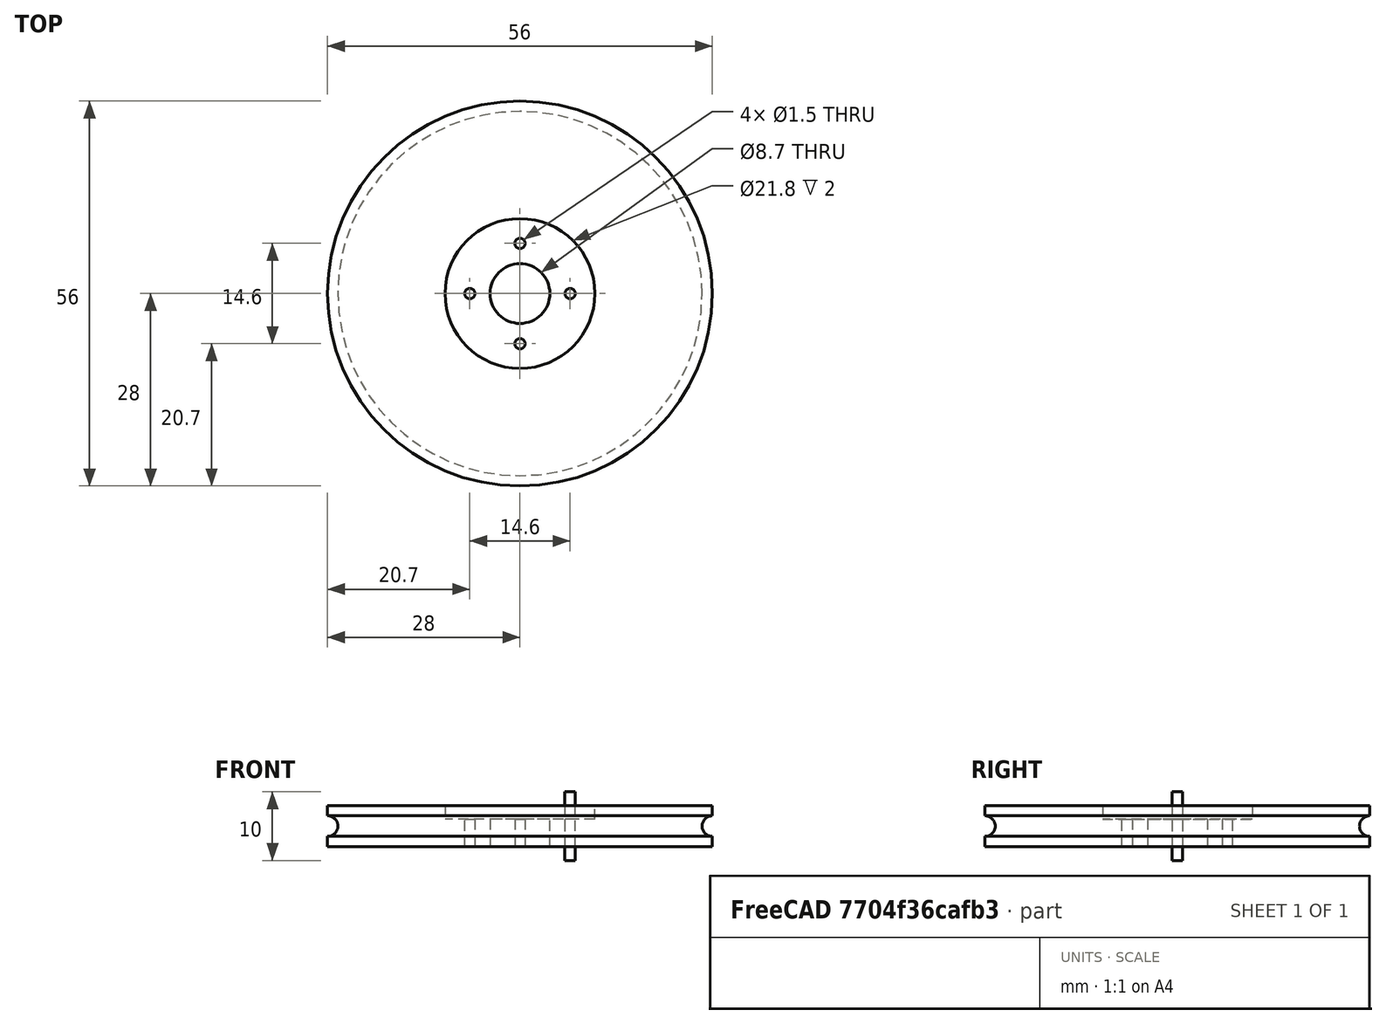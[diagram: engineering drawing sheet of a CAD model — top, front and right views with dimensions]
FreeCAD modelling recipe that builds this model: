
FCSTD DOCUMENT  (FreeCAD 0.21R33694 (Git))
Label: OJT1_T15P01_toros
License: All rights reserved
LicenseURL: https://en.wikipedia.org/wiki/All_rights_reserved
objects: Part::Cylinder×4, Part::Cut×4, Part::Torus×1, Part::FeaturePython×1
note: 9 computed .brp shape members not serialized (recipe doc carries the construction recipe); baked Part::Feature solids carry a one-line shape summary decoded from their .brp

FEATURE [Part::Cylinder] Cylinder  label="Roda base"
  Angle = 360
  AttacherType = Attacher::AttachEngine3D
  FirstAngle = 0
  Height = 6
  Placement = pos=(0,0,-3) rot=(0,0,1;0rad)
  Radius = 28
  SecondAngle = 0
FEATURE [Part::Torus] Torus  label="espai_junta_tuerca"
  Angle1 = -180
  Angle2 = 180
  Angle3 = 360
  AttacherType = Attacher::AttachEngine3D
  Radius1 = 28
  Radius2 = 1.5
FEATURE [Part::Cut] Cut  label="Roda_bàsica"
  Base = -> Cylinder
  Tool = -> Torus
FEATURE [Part::Cylinder] Cylinder001  label="corona_servo"
  Angle = 360
  AttacherType = Attacher::AttachEngine3D
  FirstAngle = 0
  Height = 10
  Placement = pos=(0,0,1) rot=(0,0,1;0rad)
  Radius = 10.9
  SecondAngle = 0
FEATURE [Part::Cut] Cut001  label="roda_amb_forat_corona"
  Base = -> Cut
  Tool = -> Cylinder001
FEATURE [Part::Cylinder] Cylinder002  label="forat_eix"
  Angle = 360
  AttacherType = Attacher::AttachEngine3D
  FirstAngle = 0
  Height = 10
  Placement = pos=(0,0,-4) rot=(0,0,1;0rad)
  Radius = 4.35
  SecondAngle = 0
FEATURE [Part::Cut] Cut002  label="roda_corona_eix"
  Base = -> Cut001
  Tool = -> Cylinder002
FEATURE [Part::Cylinder] Cylinder003  label="taladre"
  Angle = 360
  AttacherType = Attacher::AttachEngine3D
  FirstAngle = 0
  Height = 10
  Placement = pos=(7.3,0,-5) rot=(0,0,1;0rad)
  Radius = 0.75
  SecondAngle = 0
FEATURE [Part::FeaturePython] Array  # Draft array (typed FeaturePython)
  AlwaysSyncPlacement = false
  Angle = 360
  ArrayType = 1
  Axis = (0,0,1)
  Base = -> Cylinder003
  Center = (0,0,0)
  Count = 4
  ExpandArray = false
  Fuse = false
  IntervalAxis = (0,0,0)
  IntervalX = (100,0,0)
  IntervalY = (0,100,0)
  IntervalZ = (0,0,100)
  NumberCircles = 3
  NumberPolar = 4
  NumberX = 2
  NumberY = 2
  NumberZ = 1
  PlacementList = 4 placements: [(7.3,0,-5),(0,7.3,-5),(-7.3,8.93992e-16,-5),(-1.62093e-15,-7.3,-5)]
  RadialDistance = 50
  ScaleList = (4) [(1,1,1),(1,1,1),(1,1,1),(1,1,1)]
  Symmetry = 1
  TangentialDistance = 25
FEATURE [Part::Cut] Cut003  label="Roda miniskybot"
  Base = -> Cut002
  Tool = -> Array
